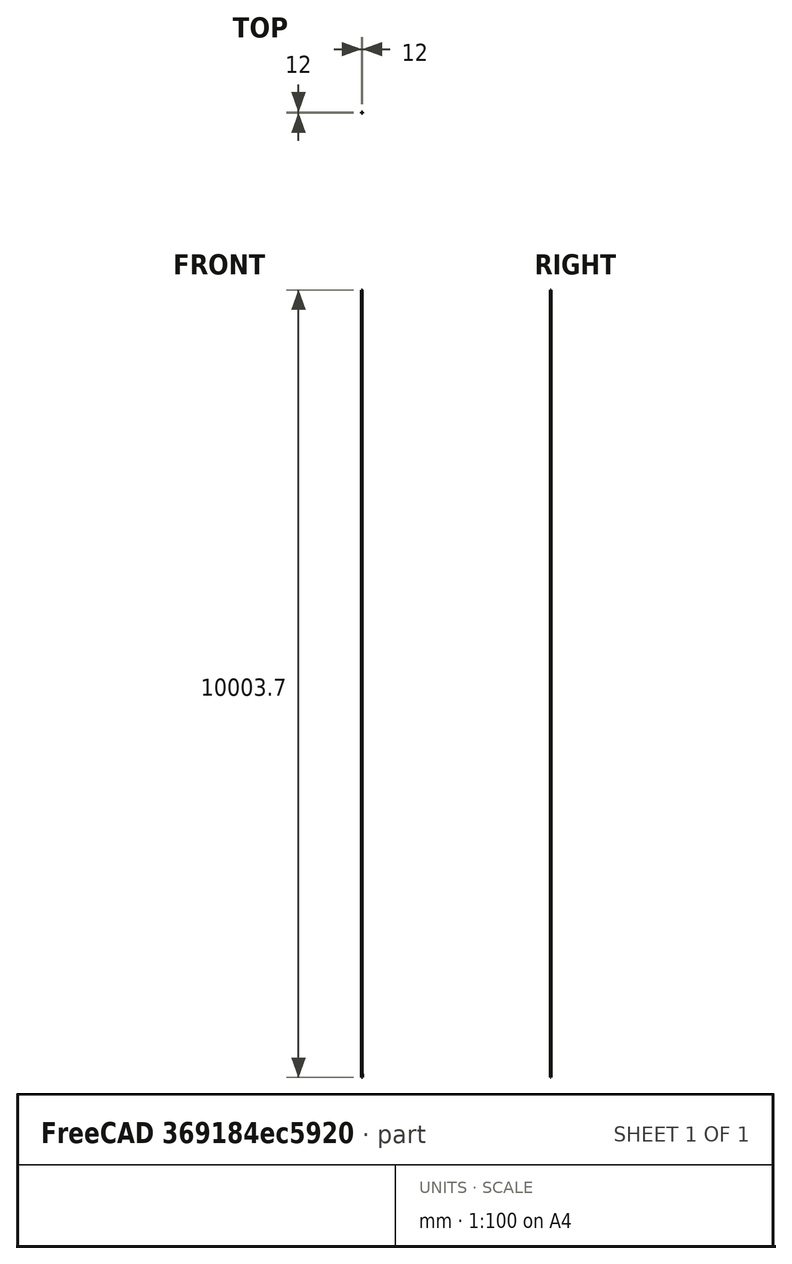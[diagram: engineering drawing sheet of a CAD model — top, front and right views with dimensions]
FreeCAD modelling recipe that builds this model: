
FCSTD DOCUMENT  (FreeCAD 0.16R)
Label: MazdaClip
License: All rights reserved
LicenseURL: http://en.wikipedia.org/wiki/All_rights_reserved
objects: Sketcher::SketchObject×6, PartDesign::Pocket×5, PartDesign::Fillet×3, PartDesign::Pad×1, Mesh::Feature×1
note: 21 computed .brp shape members not serialized (recipe doc carries the construction recipe); baked Part::Feature solids carry a one-line shape summary decoded from their .brp

FEATURE [Sketcher::SketchObject] Sketch
  sketch-geometry (4):
    g0: LineSegment StartX=-6 StartY=6 StartZ=0 EndX=6 EndY=6 EndZ=0
    g1: LineSegment StartX=6 StartY=6 StartZ=0 EndX=6 EndY=-6 EndZ=0
    g2: LineSegment StartX=6 StartY=-6 StartZ=0 EndX=-6 EndY=-6 EndZ=0
    g3: LineSegment StartX=-6 StartY=-6 StartZ=0 EndX=-6 EndY=6 EndZ=0
  constraints (11):
    c: Coincident(g0,g1)
    c: Coincident(g1,g2)
    c: Coincident(g2,g3)
    c: Coincident(g3,g0)
    c: Horizontal(g0)
    c: Horizontal(g2)
    c: Vertical(g1)
    c: Vertical(g3)
    c: Symmetric(g1,g0,g-1)
    c: Equal(g0,g1)
    c: Distance(g0) = 12
FEATURE [PartDesign::Pad] Pad
  Length = 40
  Length2 = 100
  Sketch = -> Sketch
  Type = 0
FEATURE [Sketcher::SketchObject] Sketch001
  Placement = pos=(0,0,0) rot=(1,0,0;3.14159rad)
  Support = -> Pad [Face5]
  sketch-geometry (1):
    g0: Circle CenterX=0 CenterY=0 CenterZ=0 NormalX=0 NormalY=0 NormalZ=1 Radius=2.55
  constraints (2):
    c: Coincident(g0,g-1)
    c: Radius(g0) = 2.55
FEATURE [PartDesign::Pocket] Pocket
  Length = 5
  Sketch = -> Sketch001
  Type = 1
FEATURE [Sketcher::SketchObject] Sketch002
  Placement = pos=(0,0,40) rot=(0,0,1;0rad)
  Support = -> Pocket [Face5]
  sketch-geometry (1):
    g0: Circle CenterX=0 CenterY=0 CenterZ=0 NormalX=0 NormalY=0 NormalZ=1 Radius=4.05
  constraints (2):
    c: Coincident(g0,g-1)
    c: Radius(g0) = 4.05
FEATURE [PartDesign::Pocket] Pocket001
  Length = 30
  Sketch = -> Sketch002
  Type = 0
FEATURE [Sketcher::SketchObject] Sketch003
  Placement = pos=(6,0,0) rot=(0.57735,0.57735,0.57735;2.0944rad)
  Support = -> Pocket001 [Face3]
  sketch-geometry (4):
    g0: LineSegment StartX=-5 StartY=35.36 StartZ=0 EndX=5 EndY=35.36 EndZ=0
    g1: LineSegment StartX=5 StartY=35.36 StartZ=0 EndX=5 EndY=30.36 EndZ=0
    g2: LineSegment StartX=5 StartY=30.36 StartZ=0 EndX=-5 EndY=30.36 EndZ=0
    g3: LineSegment StartX=-5 StartY=30.36 StartZ=0 EndX=-5 EndY=35.36 EndZ=0
  constraints (12):
    c: Coincident(g0,g1)
    c: Coincident(g1,g2)
    c: Coincident(g2,g3)
    c: Coincident(g3,g0)
    c: Horizontal(g0)
    c: Horizontal(g2)
    c: Vertical(g1)
    c: Vertical(g3)
    c: Distance(g1) = 5
    c: DistanceY(g0) = 35.36
    c: Symmetric(g1,g2,g-2)
    c: Distance(g2) = 10
FEATURE [PartDesign::Pocket] Pocket002
  Length = 9
  Sketch = -> Sketch003
  Type = 0
FEATURE [Sketcher::SketchObject] Sketch004
  Placement = pos=(6,0,0) rot=(0.57735,0.57735,0.57735;2.0944rad)
  Support = -> Pocket002 [Face3]
  sketch-geometry (4):
    g0: LineSegment StartX=-4 StartY=46.153 StartZ=0 EndX=4 EndY=46.153 EndZ=0
    g1: LineSegment StartX=4 StartY=46.153 StartZ=0 EndX=4 EndY=-3.69098 EndZ=0
    g2: LineSegment StartX=4 StartY=-3.69098 StartZ=0 EndX=-4 EndY=-3.69098 EndZ=0
    g3: LineSegment StartX=-4 StartY=-3.69098 StartZ=0 EndX=-4 EndY=46.153 EndZ=0
  constraints (10):
    c: Coincident(g0,g1)
    c: Coincident(g1,g2)
    c: Coincident(g2,g3)
    c: Coincident(g3,g0)
    c: Horizontal(g0)
    c: Horizontal(g2)
    c: Vertical(g1)
    c: Vertical(g3)
    c: Distance(g0) = 8
    c: Symmetric(g0,g0,g-2)
FEATURE [PartDesign::Pocket] Pocket003
  Length = 5.5
  Sketch = -> Sketch004
  Type = 0
FEATURE [Sketcher::SketchObject] Sketch005
  Placement = pos=(0,0,40) rot=(0,0,1;0rad)
  Support = -> Pocket003 [Face5]
  sketch-geometry (4):
    g0: LineSegment StartX=6.54686 StartY=11.8786 StartZ=0 EndX=4 EndY=11.8786 EndZ=0
    g1: LineSegment StartX=4 StartY=11.8786 StartZ=0 EndX=4 EndY=-8.11227 EndZ=0
    g2: LineSegment StartX=4 StartY=-8.11227 StartZ=0 EndX=6.54686 EndY=-8.11227 EndZ=0
    g3: LineSegment StartX=6.54686 StartY=-8.11227 StartZ=0 EndX=6.54686 EndY=11.8786 EndZ=0
  constraints (9):
    c: Coincident(g0,g1)
    c: Coincident(g1,g2)
    c: Coincident(g2,g3)
    c: Coincident(g3,g0)
    c: Horizontal(g0)
    c: Horizontal(g2)
    c: Vertical(g1)
    c: Vertical(g3)
    c: DistanceX(g1) = 4
FEATURE [PartDesign::Pocket] Pocket004
  Length = 5
  Sketch = -> Sketch005
  Type = 1
FEATURE [PartDesign::Fillet] Fillet
  Base = -> Pocket004 [Edge20,Edge3,Edge1,Edge5]
  Radius = 1
FEATURE [PartDesign::Fillet] Fillet001
  Base = -> Fillet [Edge39]
  Radius = 1
FEATURE [PartDesign::Fillet] Fillet002
  Base = -> Fillet001 [Edge3,Edge6]
  Radius = 0.5
FEATURE [Mesh::Feature] Mesh  label="Fillet002 (Meshed)"
